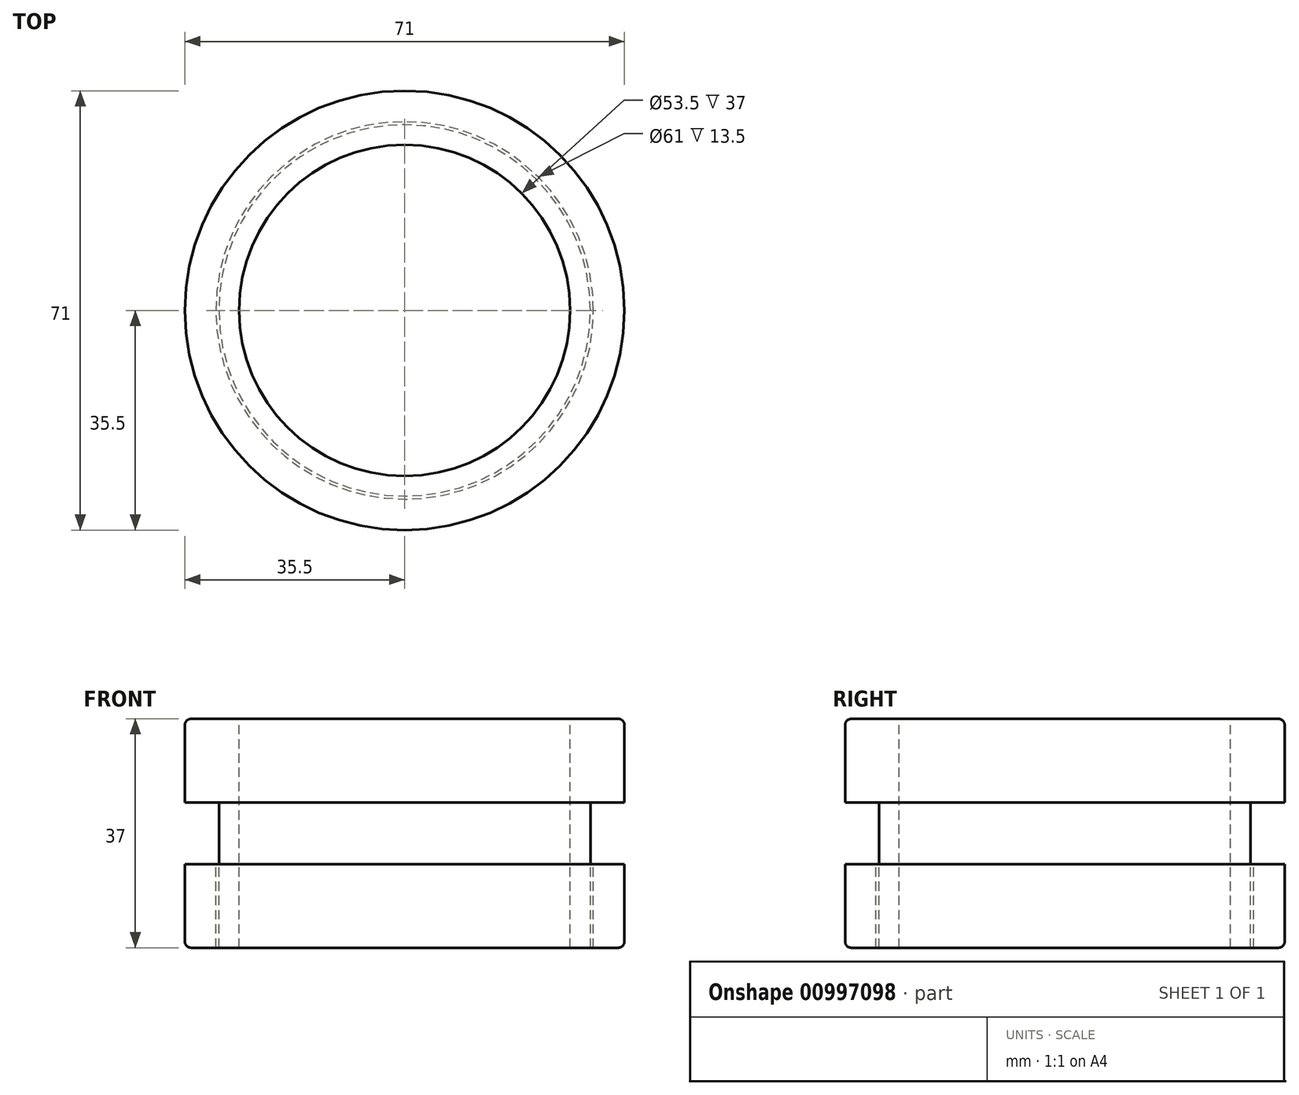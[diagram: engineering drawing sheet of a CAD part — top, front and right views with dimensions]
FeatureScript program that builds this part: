
annotation { "Feature Type Name" : "Feature", "Feature Type Description" : "" }
export const myFeature = defineFeature(function(context is Context, id is Id, definition is map)
    precondition{}
    {
        {
            var Q0;
            Q0=qCreatedBy(makeId("Front.planeOp"),FACE);
            var sketch = newSketch(context, id + "F0", { "sketchPlane" : qUnion([Q0])});
            skLineSegment(sketch, "E0", {"start": v(-35.5, 0) * mm, "end": v(-35.5, 12.5) * mm});
            skLineSegment(sketch, "E1", {"start": v(-34.5, 13.5) * mm, "end": v(-26.75, 13.5) * mm});
            skLineSegment(sketch, "E2", {"start": v(-26.75, 13.5) * mm, "end": v(-26.75, -23.5) * mm});
            skLineSegment(sketch, "E3", {"start": v(-26.75, -23.5) * mm, "end": v(-30, -23.5) * mm});
            skLineSegment(sketch, "E4", {"start": v(-30, -23.5) * mm, "end": v(-30, 0) * mm});
            skLineSegment(sketch, "E5", {"start": v(-30, 0) * mm, "end": v(-35.5, 0) * mm});
            skLineSegment(sketch, "E6", {"start": v(0, 40.57) * mm, "end": v(0, -41.06) * mm, "construction": true});
            skPoint(sketch, "E7.visualSharp", {"position": v(-35.5, 13.5) * mm});
            skArc(sketch, "E7.filletArc", {"start": v(-34.5, 13.5) * mm, "mid": v(-35.2, 13.2) * mm, "end": v(-35.5, 12.5) * mm});
            skLineSegment(sketch, "E8", {"start": v(-30.5, -10) * mm, "end": v(-30.5, -23.5) * mm});
            skLineSegment(sketch, "E9", {"start": v(-30.5, -23.5) * mm, "end": v(-34.5, -23.5) * mm});
            skLineSegment(sketch, "E10", {"start": v(-35.5, -22.5) * mm, "end": v(-35.5, -10) * mm});
            skLineSegment(sketch, "E11", {"start": v(-35.5, -10) * mm, "end": v(-30.5, -10) * mm});
            skPoint(sketch, "E12.visualSharp", {"position": v(-35.5, -23.5) * mm});
            skArc(sketch, "E12.filletArc", {"start": v(-35.5, -22.5) * mm, "mid": v(-35.2, -23.2) * mm, "end": v(-34.5, -23.5) * mm});
            skSolve(sketch);
        }
        {
            var Q0;
            Q0 = qSketchRegion(id + "F0", true);
            var Q1;
            Q1=sQuery(id+"F0.wireOp",EDGE,"E6");
            revolve(context, id + "F1", {"surfaceOperationType" : NewSurfaceOperationType.NEW, "entities" : qUnion([Q0]), "axis" : qUnion([Q1]), "revolveType" : RevolveType.FULL});
        }
    });
